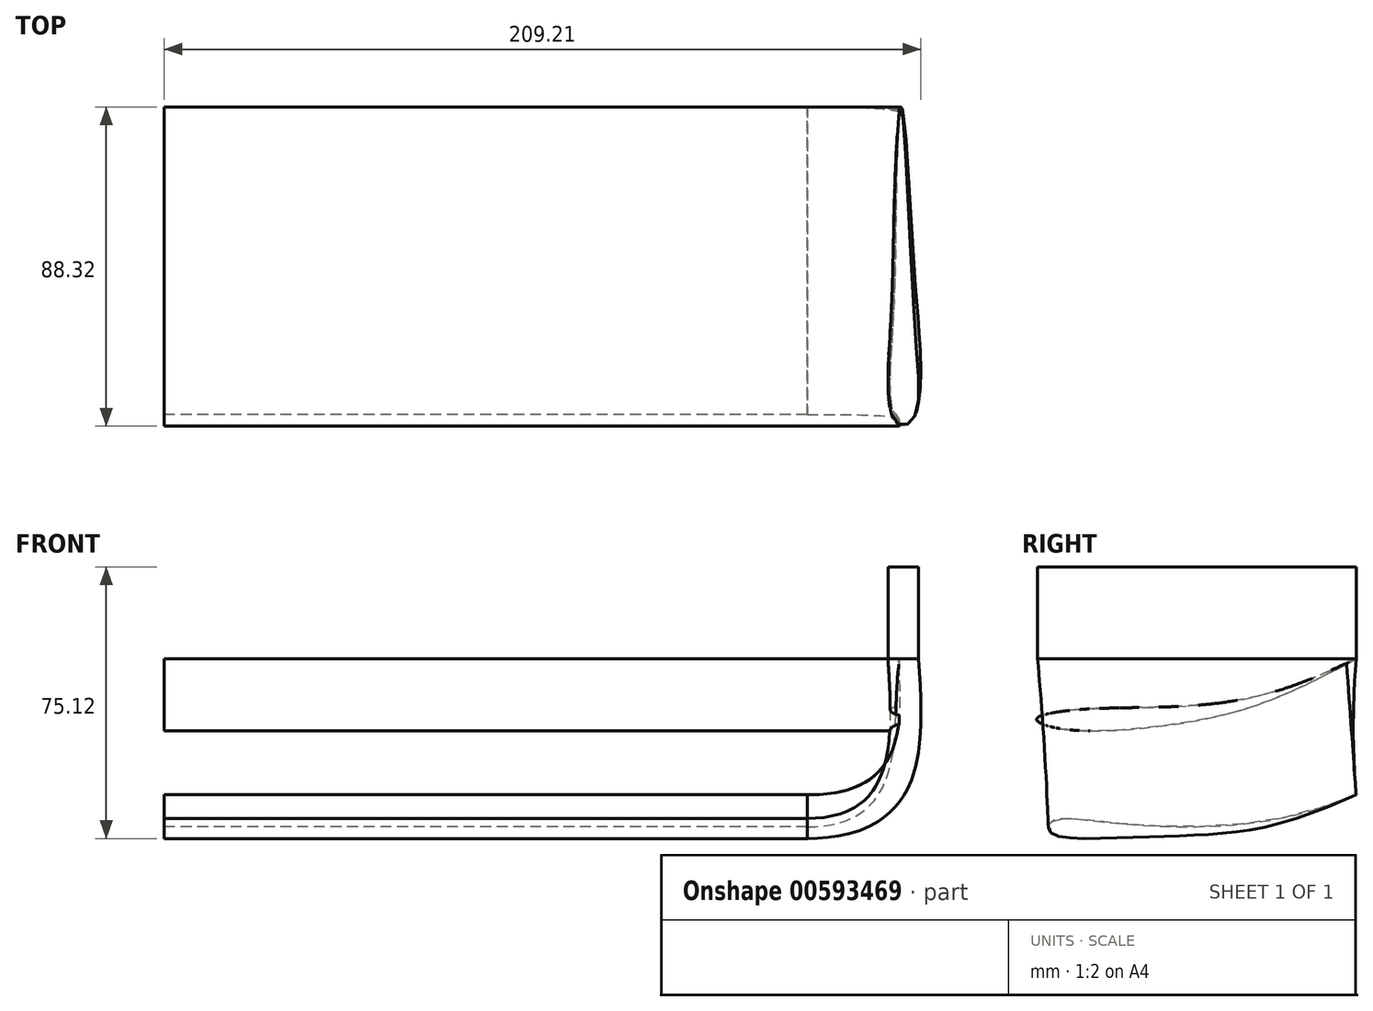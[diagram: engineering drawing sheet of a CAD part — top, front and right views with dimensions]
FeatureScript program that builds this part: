
annotation { "Feature Type Name" : "Feature", "Feature Type Description" : "" }
export const myFeature = defineFeature(function(context is Context, id is Id, definition is map)
    precondition{}
    {
        {
            var Q0;
            Q0=qCreatedBy(makeId("Right.planeOp"),FACE);
            var sketch = newSketch(context, id + "F0", { "sketchPlane" : qUnion([Q0])});
            skFitSpline(sketch, "E0", {"points": [v(0, 0) * mm, v(-19.96, -8.3) * mm, v(-55.22, -13.4) * mm, v(-79.37, -14.3) * mm, v(-88.3, -16.68) * mm, v(-81.2, -19.41) * mm, v(-48.02, -17.77) * mm, v(-18.68, -9.39) * mm, v(0, 0) * mm]});
            skSolve(sketch);
        }
        {
            var Q0;
            Q0 = qSketchRegion(id + "F0", true);
            extrude(context, id + "F1", {"entities" : qUnion([Q0]), "depth" : 203.2 * mm, "offsetDistance" : 25.4 * mm});
        }
        {
            var Q0;
            Q0=qCreatedBy(makeId("Right.planeOp"),FACE);
            var sketch = newSketch(context, id + "F2", { "sketchPlane" : qUnion([Q0])});
            skFitSpline(sketch, "E1", {"points": [v(0, -37.64) * mm, v(-19.45, -43.83) * mm, v(-68.48, -45.3) * mm, v(-84.33, -45.1) * mm, v(-84.52, -48.02) * mm, v(-66.1, -49.48) * mm, v(-40.78, -48.57) * mm, v(-17.26, -44.38) * mm, v(0, -37.64) * mm]});
            skSolve(sketch);
        }
        {
            var Q0;
            Q0 = qSketchRegion(id + "F2", true);
            extrude(context, id + "F3", {"entities" : qUnion([Q0]), "depth" : 177.8 * mm, "offsetDistance" : 25.4 * mm});
        }
        {
            var Q0;
            Q0=qCreatedBy(makeId("Top.planeOp"),FACE);
            var sketch = newSketch(context, id + "F4", { "sketchPlane" : qUnion([Q0])});
            skFitSpline(sketch, "E2", {"points": [v(203.66, 0) * mm, v(201.84, -26.8) * mm, v(201.01, -56.9) * mm, v(201.34, -85.75) * mm, v(204.65, -88.07) * mm, v(207.63, -85.42) * mm, v(207.3, -56.97) * mm, v(203.66, 0) * mm]});
            skSolve(sketch);
        }
        {
            var Q1;
            Q1=makeQuery(id+"F3.opExtrude","CAP_FACE",FACE,{"disambiguationData":[OSD([sQuery(id+"F2.wireOp",EDGE,"E1")])],"isStart":false});
            var Q2;
            Q2=makeQuery(id+"F4.imprint","IMPRINT",FACE,{"disambiguationData":[TD([[makeQuery(id+"F4.imprint","IMPRINT",EDGE,{"derivedFrom":sQuery(id+"F4.wireOp",EDGE,"E2")}),1.0]])]});
            loft(context, id + "F5", {"operationType" : NewBodyOperationType.ADD, "startCondition" : LoftEndDerivativeType.NORMAL_TO_PROFILE, "startMagnitude" : 3, "sheetProfilesArray" : [{ "sheetProfileEntities" : qUnion([Q1]) }, { "sheetProfileEntities" : qUnion([Q2]) }]});
        }
        {
            var Q0;
            Q0=makeQuery(id+"F5.opLoft","CAP_FACE",FACE,{"disambiguationData":[OSD([makeQuery(id+"F4.imprint","IMPRINT",FACE,{"disambiguationData":[TD([[makeQuery(id+"F4.imprint","IMPRINT",EDGE,{"derivedFrom":sQuery(id+"F4.wireOp",EDGE,"E2")}),1.0]])]})])],"isStart":true});
            extrude(context, id + "F6", {"entities" : qUnion([Q0]), "operationType" : NewBodyOperationType.ADD, "depth" : 25.4 * mm, "offsetDistance" : 25.4 * mm});
        }
    });
